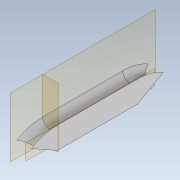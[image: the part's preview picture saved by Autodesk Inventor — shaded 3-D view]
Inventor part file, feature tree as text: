
AUTODESK INVENTOR PART (.ipt)
format: ipt  version: 2021 (Build 250183000, 183)  size: 131,584 bytes
history: native  units: in
note: dims shown in document units (in); Inventor stores cm internally (conversion verified against a paired STEP export)
features: sketch x3, move_body x2, extrude x1, plane x1, sweep x1, direct_edit x1
ambient origin geometry x8: Origin, YZ Plane, XZ Plane, XY Plane, X Axis, Y Axis, Z Axis, Center Point
bodies: Solid1 (feature_tree)
feature tree (9):
  extrude  "Extrusion1"  Depth=6.0in
  plane  "Work Plane1"
  sweep  "Sweep1"
  direct_edit  "Direct Edit1"
  sketch  "Sketch1"  dims[d0=5.5in d2=6.0in]
  sketch  "Sketch2"  dims[d3=1.0in d4=1.0in d5=1.0in d6=0.0in d7=-0.5in d8=0.5in d9=0.5in d10=0.0in d11=0.0in d12=0.0in d13=0.0in d14=0.3899in d15=0.0in d16=0.0in d17=0.3899in]
  sketch  "3D Sketch1"
  move_body  "Move1"
  move_body  "Move2"
